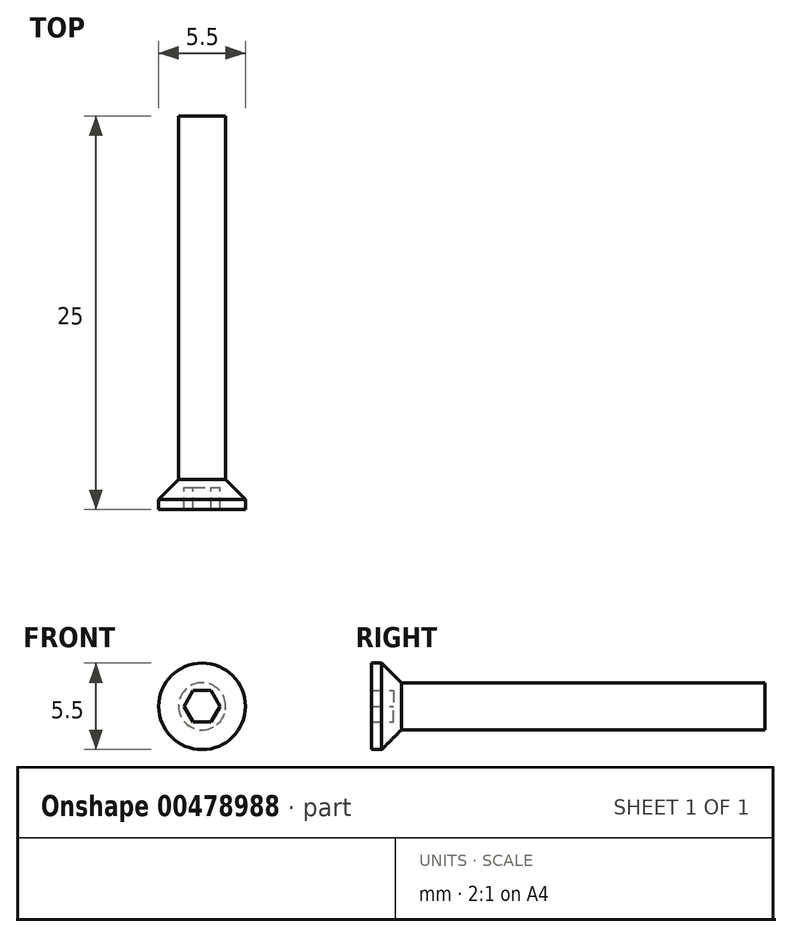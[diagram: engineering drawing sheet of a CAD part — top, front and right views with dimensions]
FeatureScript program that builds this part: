
annotation { "Feature Type Name" : "Feature", "Feature Type Description" : "" }
export const myFeature = defineFeature(function(context is Context, id is Id, definition is map)
    precondition{}
    {
        {
            var Q0;
            Q0=qCreatedBy(makeId("Front.planeOp"),FACE);
            var sketch = newSketch(context, id + "F0", { "sketchPlane" : qUnion([Q0])});
            skCircle(sketch, "E0", {"center": v(0, 0) * mm, "radius": 2.75 * mm});
            skSolve(sketch);
        }
        {
            var Q0;
            Q0 = qSketchRegion(id + "F0", true);
            extrude(context, id + "F1", {"entities" : qUnion([Q0]), "depth" : 1.9 * mm});
        }
        {
            var Q0;
            Q0=makeQuery(id+"F1.opExtrude","CAP_FACE",FACE,{"disambiguationData":[OSD([sQuery(id+"F0.wireOp",EDGE,"E0")])],"isStart":true});
            var sketch = newSketch(context, id + "F2", { "sketchPlane" : qUnion([Q0])});
            skCircle(sketch, "E1", {"center": v(0, 0) * mm, "radius": 1.5 * mm});
            skSolve(sketch);
        }
        {
            var Q0;
            Q0 = qSketchRegion(id + "F2", true);
            extrude(context, id + "F3", {"entities" : qUnion([Q0]), "operationType" : NewBodyOperationType.ADD, "depth" : 23.1 * mm});
        }
        {
            var Q0;
            Q0=qCreatedBy(makeId("Front.planeOp"),FACE);
            var sketch = newSketch(context, id + "F4", { "sketchPlane" : qUnion([Q0])});
            skCircle(sketch, "E2.cCircle", {"center": v(0, 0) * mm, "radius": 1 * mm, "construction": true});
            skLineSegment(sketch, "E2.0", {"start": v(0.58, 1) * mm, "end": v(1.15, 0) * mm});
            skLineSegment(sketch, "E2.1", {"start": v(1.15, 0) * mm, "end": v(0.58, -1) * mm});
            skLineSegment(sketch, "E2.2", {"start": v(0.58, -1) * mm, "end": v(-0.58, -1) * mm});
            skLineSegment(sketch, "E2.3", {"start": v(-0.58, -1) * mm, "end": v(-1.15, 0) * mm});
            skLineSegment(sketch, "E2.4", {"start": v(-1.15, 0) * mm, "end": v(-0.58, 1) * mm});
            skLineSegment(sketch, "E2.5", {"start": v(-0.58, 1) * mm, "end": v(0.58, 1) * mm});
            skPoint(sketch, "E2.0.midPoint", {"position": v(0.87, 0.5) * mm});
            skSolve(sketch);
        }
        {
            var Q0;
            Q0 = qSketchRegion(id + "F4", true);
            extrude(context, id + "F5", {"entities" : qUnion([Q0]), "operationType" : NewBodyOperationType.REMOVE, "depth" : 5 * mm, "hasSecondDirection" : true, "secondDirectionOppositeDirection" : false, "secondDirectionDepth" : 0.5 * mm});
        }
        {
            var Q0;
            Q0=makeQuery(id+"F1.opExtrude","CAP_EDGE",EDGE,{"disambiguationData":[OSD([sQuery(id+"F0.wireOp",EDGE,"E0")])],"isStart":true});
            chamfer(context, id + "F6", {"entities" : qUnion([Q0]), "chamferType" : ChamferType.OFFSET_ANGLE, "width" : ((5.5 - 3) / 2) * mm, "oppositeDirection" : false, "angle" : 45 * degree, "tangentPropagation" : true});
        }
    });
